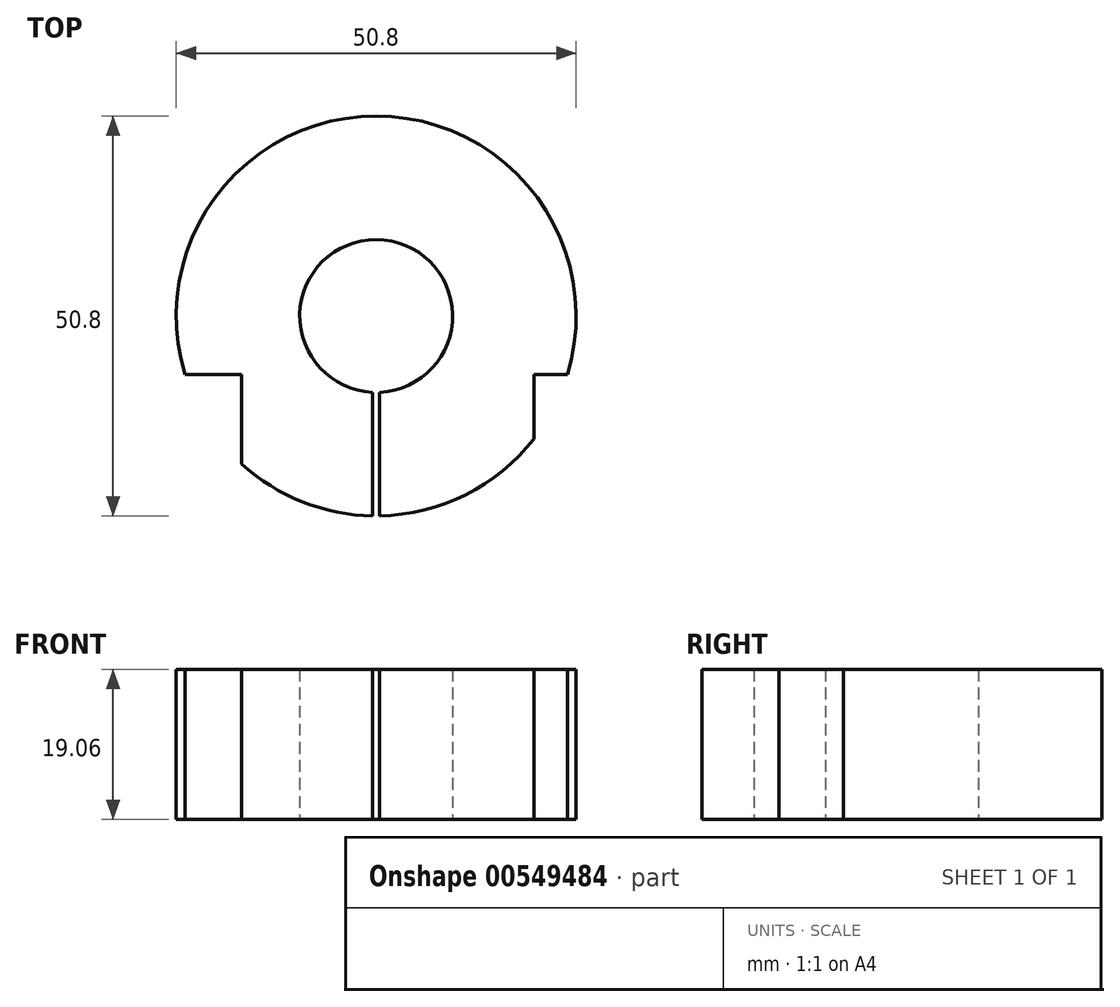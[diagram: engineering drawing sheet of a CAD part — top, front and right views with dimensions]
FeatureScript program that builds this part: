
annotation { "Feature Type Name" : "Feature", "Feature Type Description" : "" }
export const myFeature = defineFeature(function(context is Context, id is Id, definition is map)
    precondition{}
    {
        {
            var Q0;
            Q0=qCreatedBy(makeId("Top.planeOp"),FACE);
            var sketch = newSketch(context, id + "F0", { "sketchPlane" : qUnion([Q0])});
            skCircle(sketch, "E0", {"center": v(0, 0) * mm, "radius": 9.59 * mm});
            skCircle(sketch, "E1", {"center": v(0, 0) * mm, "radius": 25.4 * mm});
            skSolve(sketch);
        }
        {
            var Q0;
            Q0=makeQuery(id+"F0.imprint","IMPRINT",FACE,{"disambiguationData":[TD([[makeQuery(id+"F0.imprint","IMPRINT",EDGE,{"derivedFrom":sQuery(id+"F0.wireOp",EDGE,"E0")}),-1.0]])]});
            extrude(context, id + "F1", {"entities" : qUnion([Q0]), "endBound" : BoundingType.SYMMETRIC, "depth" : 19.05 * mm, "offsetDistance" : 25.4 * mm});
        }
        {
            var Q0;
            Q0=qCreatedBy(makeId("Top.planeOp"),FACE);
            var sketch = newSketch(context, id + "F2", { "sketchPlane" : qUnion([Q0])});
            skLineSegment(sketch, "E2.bottom", {"start": v(-17.08, -7.44) * mm, "end": v(-28.5, -7.44) * mm});
            skLineSegment(sketch, "E2.top", {"start": v(-17.08, -19.3) * mm, "end": v(-28.5, -19.3) * mm});
            skLineSegment(sketch, "E2.left", {"start": v(-17.08, -7.44) * mm, "end": v(-17.08, -19.3) * mm});
            skLineSegment(sketch, "E2.right", {"start": v(-28.5, -7.44) * mm, "end": v(-28.5, -19.3) * mm});
            skLineSegment(sketch, "E3.bottom", {"start": v(20.04, -7.44) * mm, "end": v(36.7, -7.44) * mm});
            skLineSegment(sketch, "E3.top", {"start": v(20.04, -22.8) * mm, "end": v(36.7, -22.8) * mm});
            skLineSegment(sketch, "E3.left", {"start": v(20.04, -7.44) * mm, "end": v(20.04, -22.8) * mm});
            skLineSegment(sketch, "E3.right", {"start": v(36.7, -7.44) * mm, "end": v(36.7, -22.8) * mm});
            skSolve(sketch);
        }
        {
            var Q0;
            Q0=makeQuery(id+"F2.imprint","IMPRINT",FACE,{"disambiguationData":[TD([[makeQuery(id+"F2.imprint","IMPRINT",EDGE,{"derivedFrom":sQuery(id+"F2.wireOp",EDGE,"E2.bottom")}),1.0]])]});
            var Q1;
            Q1=makeQuery(id+"F2.imprint","IMPRINT",FACE,{"disambiguationData":[TD([[makeQuery(id+"F2.imprint","IMPRINT",EDGE,{"derivedFrom":sQuery(id+"F2.wireOp",EDGE,"E3.bottom")}),-1.0]])]});
            extrude(context, id + "F3", {"entities" : qUnion([Q0, Q1]), "operationType" : NewBodyOperationType.REMOVE, "endBound" : BoundingType.SYMMETRIC, "oppositeDirection" : true, "depth" : 35.56 * mm, "offsetDistance" : 25.4 * mm});
        }
        {
            var Q0;
            Q0=qCreatedBy(makeId("Top.planeOp"),FACE);
            var sketch = newSketch(context, id + "F4", { "sketchPlane" : qUnion([Q0])});
            skLineSegment(sketch, "E4.bottom", {"start": v(0.46, -6.05) * mm, "end": v(-0.46, -6.05) * mm});
            skLineSegment(sketch, "E4.top", {"start": v(0.46, -28.84) * mm, "end": v(-0.46, -28.84) * mm});
            skLineSegment(sketch, "E4.left", {"start": v(0.46, -6.05) * mm, "end": v(0.46, -28.84) * mm});
            skLineSegment(sketch, "E4.right", {"start": v(-0.46, -6.05) * mm, "end": v(-0.46, -28.84) * mm});
            skPoint(sketch, "E4.middle", {"position": v(0, -17.44) * mm});
            skSolve(sketch);
        }
        {
            var Q0;
            Q0=makeQuery(id+"F4.imprint","IMPRINT",FACE,{"disambiguationData":[TD([[makeQuery(id+"F4.imprint","IMPRINT",EDGE,{"derivedFrom":sQuery(id+"F4.wireOp",EDGE,"E4.bottom")}),1.0]])]});
            extrude(context, id + "F5", {"entities" : qUnion([Q0]), "operationType" : NewBodyOperationType.REMOVE, "endBound" : BoundingType.SYMMETRIC, "depth" : 31.2 * mm, "offsetDistance" : 25.4 * mm});
        }
        {
            var Q0;
            Q0=qCreatedBy(makeId("Top.planeOp"),FACE);
            var sketch = newSketch(context, id + "F6", { "sketchPlane" : qUnion([Q0])});
            skCircle(sketch, "E5", {"center": v(0, 0) * mm, "radius": 9.72 * mm});
            skSolve(sketch);
        }
        {
            var Q0;
            Q0 = qSketchRegion(id + "F6", true);
            extrude(context, id + "F7", {"entities" : qUnion([Q0]), "operationType" : NewBodyOperationType.REMOVE, "endBound" : BoundingType.SYMMETRIC, "depth" : 76.2 * mm, "offsetDistance" : 25.4 * mm});
        }
    });
